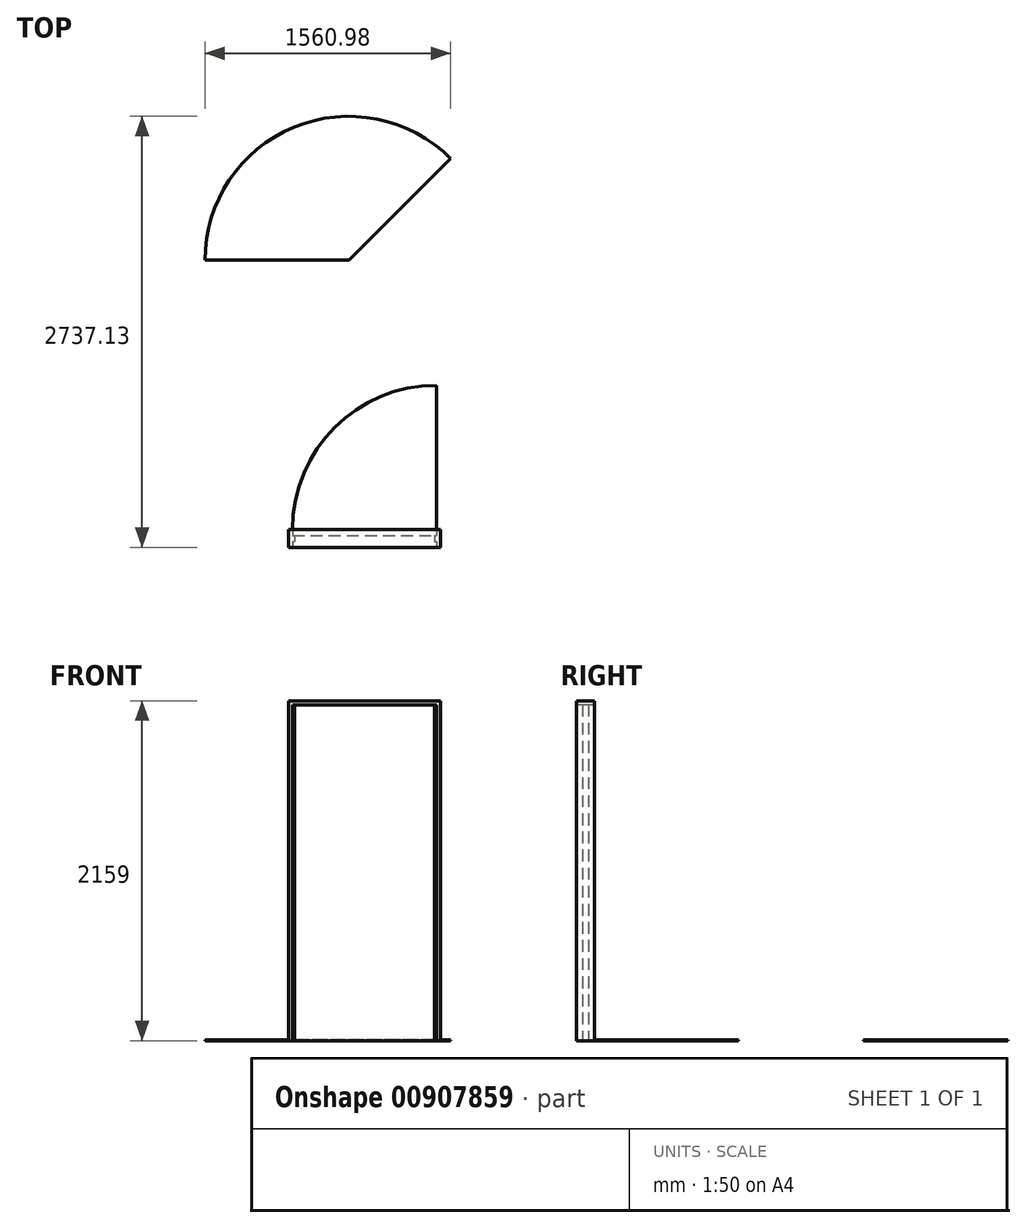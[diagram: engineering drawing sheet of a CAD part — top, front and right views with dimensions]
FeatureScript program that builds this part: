
annotation { "Feature Type Name" : "Feature", "Feature Type Description" : "" }
export const myFeature = defineFeature(function(context is Context, id is Id, definition is map)
    precondition{}
    {
        {
            var Q0;
            Q0=qCreatedBy(makeId("Top.planeOp"),FACE);
            var sketch = newSketch(context, id + "F0", { "sketchPlane" : qUnion([Q0])});
            skLineSegment(sketch, "E0.bottom", {"start": v(939.8, 57.15) * mm, "end": v(965.2, 57.15) * mm});
            skLineSegment(sketch, "E0.top", {"start": v(939.8, -57.15) * mm, "end": v(965.2, -57.15) * mm});
            skLineSegment(sketch, "E0.left", {"start": v(939.8, 57.15) * mm, "end": v(939.8, -57.15) * mm});
            skLineSegment(sketch, "E0.right", {"start": v(965.2, 57.15) * mm, "end": v(965.2, -57.15) * mm});
            skLineSegment(sketch, "E1.bottom", {"start": v(0, 57.15) * mm, "end": v(25.4, 57.15) * mm});
            skLineSegment(sketch, "E1.top", {"start": v(0, -57.15) * mm, "end": v(25.4, -57.15) * mm});
            skLineSegment(sketch, "E1.left", {"start": v(0, 57.15) * mm, "end": v(0, -57.15) * mm});
            skLineSegment(sketch, "E1.right", {"start": v(25.4, 57.15) * mm, "end": v(25.4, -57.15) * mm});
            skLineSegment(sketch, "E2.bottom", {"start": v(25.4, 19.05) * mm, "end": v(38.1, 19.05) * mm});
            skLineSegment(sketch, "E2.top", {"start": v(25.4, -19.05) * mm, "end": v(38.1, -19.05) * mm});
            skLineSegment(sketch, "E2.left", {"start": v(25.4, 19.05) * mm, "end": v(25.4, -19.05) * mm});
            skLineSegment(sketch, "E2.right", {"start": v(38.1, 19.05) * mm, "end": v(38.1, -19.05) * mm});
            skPoint(sketch, "E3", {"position": v(25.4, 0) * mm});
            skLineSegment(sketch, "E4.bottom", {"start": v(927.1, 19.05) * mm, "end": v(939.8, 19.05) * mm});
            skLineSegment(sketch, "E4.top", {"start": v(927.1, -19.05) * mm, "end": v(939.8, -19.05) * mm});
            skLineSegment(sketch, "E4.left", {"start": v(927.1, 19.05) * mm, "end": v(927.1, -19.05) * mm});
            skLineSegment(sketch, "E4.right", {"start": v(939.8, 19.05) * mm, "end": v(939.8, -19.05) * mm});
            skPoint(sketch, "E5", {"position": v(939.8, 0) * mm});
            skLineSegment(sketch, "E6.bottom", {"start": v(25.4, 57.15) * mm, "end": v(939.8, 57.15) * mm});
            skLineSegment(sketch, "E6.top", {"start": v(25.4, 19.05) * mm, "end": v(939.8, 19.05) * mm});
            skLineSegment(sketch, "E6.left", {"start": v(25.4, 57.15) * mm, "end": v(25.4, 19.05) * mm});
            skLineSegment(sketch, "E6.right", {"start": v(939.8, 57.15) * mm, "end": v(939.8, 19.05) * mm});
            skArc(sketch, "E7", {"start": v(939.8, 971.55) * mm, "mid": v(293.22, 703.73) * mm, "end": v(25.4, 57.15) * mm});
            skLineSegment(sketch, "E8", {"start": v(939.8, 57.15) * mm, "end": v(939.8, 971.55) * mm});
            skLineSegment(sketch, "E9.bottom", {"start": v(-530.77, 1765.58) * mm, "end": v(383.63, 1765.58) * mm});
            skArc(sketch, "E10", {"start": v(1030.21, 2412.16) * mm, "mid": v(33.7, 2610.38) * mm, "end": v(-530.77, 1765.58) * mm});
            skLineSegment(sketch, "E11", {"start": v(383.63, 1765.58) * mm, "end": v(1030.21, 2412.16) * mm});
            skSolve(sketch);
        }
        {
            var Q0;
            {var subQ3=sQuery(id+"F0.wireOp",EDGE,"E1.bottom");Q0=makeQuery(id+"F0.imprint","IMPRINT",FACE,{"disambiguationData":[TD([[makeQuery(id+"F0.imprint","IMPRINT",EDGE,{"derivedFrom":subQ3}),-1.0]])]});}
            var Q1;
            {var subQ2=sQuery(id+"F0.wireOp",EDGE,"E2.bottom");Q1=makeQuery(id+"F0.imprint","IMPRINT",FACE,{"disambiguationData":[TD([[makeQuery(id+"F0.imprint","IMPRINT",EDGE,{"derivedFrom":subQ2}),-1.0]])]});}
            var Q2;
            {var subQ1=sQuery(id+"F0.wireOp",EDGE,"E0.bottom");Q2=makeQuery(id+"F0.imprint","IMPRINT",FACE,{"disambiguationData":[TD([[makeQuery(id+"F0.imprint","IMPRINT",EDGE,{"derivedFrom":subQ1}),-1.0]])]});}
            var Q3;
            {var subQ2=sQuery(id+"F0.wireOp",EDGE,"E4.bottom");Q3=makeQuery(id+"F0.imprint","IMPRINT",FACE,{"disambiguationData":[TD([[makeQuery(id+"F0.imprint","IMPRINT",EDGE,{"derivedFrom":subQ2}),-1.0]])]});}
            extrude(context, id + "F1", {"entities" : qUnion([Q0, Q1, Q2, Q3]), "depth" : 2133.6 * mm, "offsetDistance" : 25.4 * mm});
        }
        {
            var Q0;
            Q0=makeQuery(id+"F1.opExtrude","SWEPT_FACE",FACE,{"disambiguationData":[OSD([sQuery(id+"F0.wireOp",EDGE,"E1.left")])]});
            var sketch = newSketch(context, id + "F2", { "sketchPlane" : qUnion([Q0])});
            skLineSegment(sketch, "E12.bottom", {"start": v(-57.15, 2159) * mm, "end": v(57.15, 2159) * mm});
            skLineSegment(sketch, "E12.top", {"start": v(-57.15, 2133.6) * mm, "end": v(57.15, 2133.6) * mm});
            skLineSegment(sketch, "E12.left", {"start": v(-57.15, 2159) * mm, "end": v(-57.15, 2133.6) * mm});
            skLineSegment(sketch, "E12.right", {"start": v(57.15, 2159) * mm, "end": v(57.15, 2133.6) * mm});
            skLineSegment(sketch, "E13.bottom", {"start": v(-19.05, 2133.6) * mm, "end": v(19.05, 2133.6) * mm});
            skLineSegment(sketch, "E13.top", {"start": v(-19.05, 2120.9) * mm, "end": v(19.05, 2120.9) * mm});
            skLineSegment(sketch, "E13.left", {"start": v(-19.05, 2133.6) * mm, "end": v(-19.05, 2120.9) * mm});
            skLineSegment(sketch, "E13.right", {"start": v(19.05, 2133.6) * mm, "end": v(19.05, 2120.9) * mm});
            skPoint(sketch, "E14", {"position": v(0, 2133.6) * mm});
            skSolve(sketch);
        }
        {
            var Q0;
            Q0=makeQuery(id+"F2.imprint","IMPRINT",FACE,{"disambiguationData":[TD([[makeQuery(id+"F2.imprint","IMPRINT",EDGE,{"derivedFrom":sQuery(id+"F2.wireOp",EDGE,"E13.bottom")}),-1.0]])]});
            var Q1;
            Q1=makeQuery(id+"F2.imprint","IMPRINT",FACE,{"disambiguationData":[TD([[makeQuery(id+"F2.imprint","IMPRINT",EDGE,{"derivedFrom":sQuery(id+"F2.wireOp",EDGE,"E12.bottom")}),-1.0]])]});
            extrude(context, id + "F3", {"entities" : qUnion([Q0, Q1]), "operationType" : NewBodyOperationType.ADD, "oppositeDirection" : true, "depth" : 965.2 * mm, "offsetDistance" : 25.4 * mm});
        }
        {
            var Q0;
            {var subQ1=sQuery(id+"F0.wireOp",EDGE,"E2.bottom");Q0=makeQuery(id+"F0.imprint","IMPRINT",FACE,{"disambiguationData":[TD([[makeQuery(id+"F0.imprint","IMPRINT",EDGE,{"derivedFrom":subQ1}),1.0]])]});}
            extrude(context, id + "F4", {"entities" : qUnion([Q0]), "depth" : 2133.6 * mm, "offsetDistance" : 25.4 * mm});
        }
        {
            var Q0;
            Q0=makeQuery(id+"F0.imprint","IMPRINT",FACE,{"disambiguationData":[TD([[makeQuery(id+"F0.imprint","IMPRINT",EDGE,{"derivedFrom":sQuery(id+"F0.wireOp",EDGE,"E6.bottom")}),1.0]])]});
            var Q1;
            Q1=makeQuery(id+"F0.imprint","IMPRINT",FACE,{"disambiguationData":[TD([[makeQuery(id+"F0.imprint","IMPRINT",EDGE,{"derivedFrom":sQuery(id+"F0.wireOp",EDGE,"E9.bottom")}),1.0]])]});
            extrude(context, id + "F5", {"entities" : qUnion([Q0, Q1]), "depth" : 6.35 * mm, "offsetDistance" : 25.4 * mm});
        }
    });
